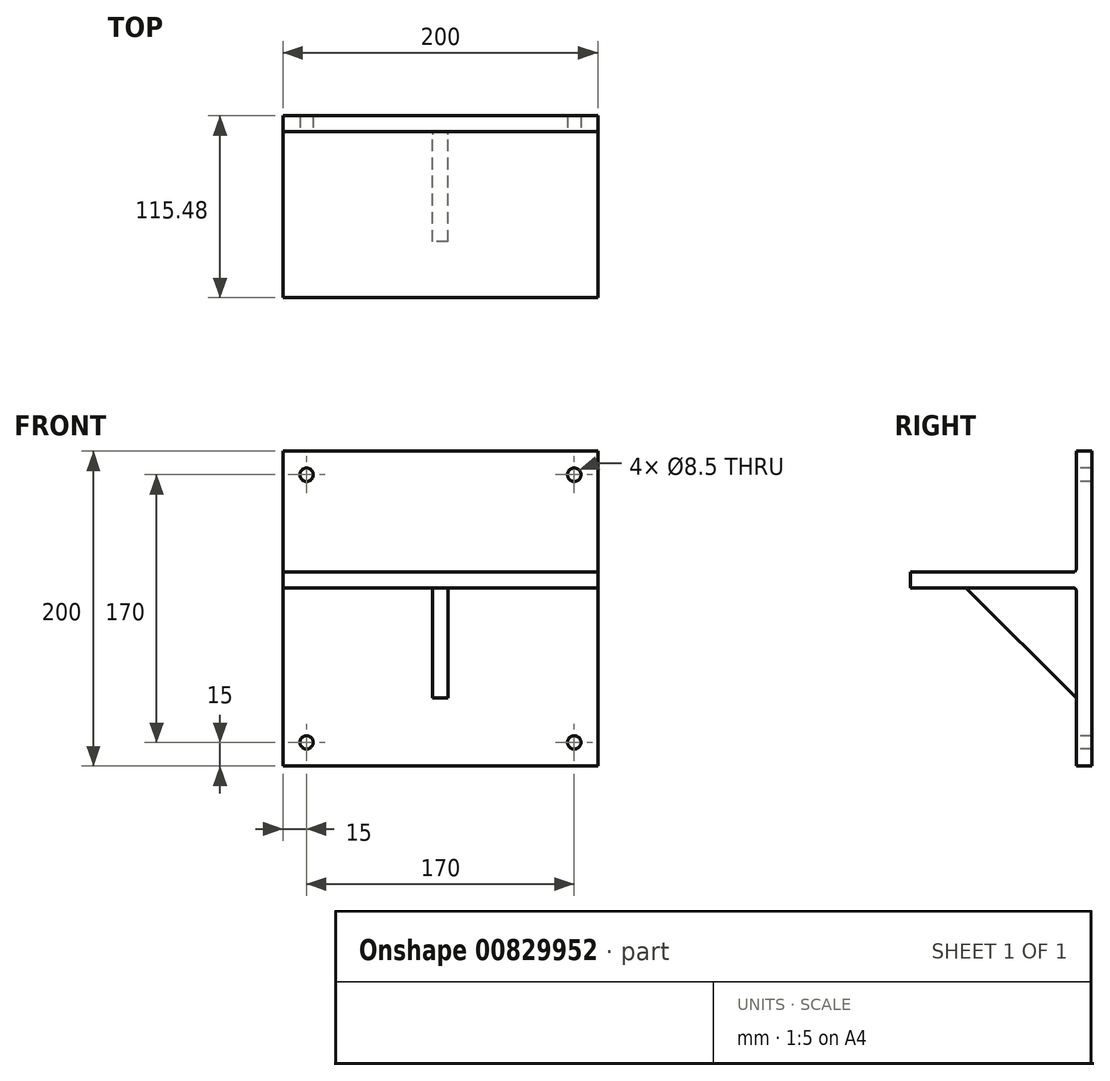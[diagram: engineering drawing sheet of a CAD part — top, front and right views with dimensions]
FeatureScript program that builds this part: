
annotation { "Feature Type Name" : "Feature", "Feature Type Description" : "" }
export const myFeature = defineFeature(function(context is Context, id is Id, definition is map)
    precondition{}
    {
        {
            var Q0;
            Q0=qCreatedBy(makeId("Right.planeOp"),FACE);
            var sketch = newSketch(context, id + "F0", { "sketchPlane" : qUnion([Q0])});
            skLineSegment(sketch, "E0", {"start": v(5, 81.8) * mm, "end": v(5, -118.2) * mm});
            skLineSegment(sketch, "E1", {"start": v(5, -118.2) * mm, "end": v(-5, -118.2) * mm});
            skLineSegment(sketch, "E2", {"start": v(5, 81.8) * mm, "end": v(-5, 81.8) * mm});
            skLineSegment(sketch, "E3", {"start": v(-5, 81.8) * mm, "end": v(-5, 5) * mm});
            skLineSegment(sketch, "E4", {"start": v(-5, -118.2) * mm, "end": v(-5, -5) * mm});
            skLineSegment(sketch, "E5", {"start": v(-5, -5) * mm, "end": v(-110.48, -5) * mm});
            skLineSegment(sketch, "E6", {"start": v(-110.48, -5) * mm, "end": v(-110.48, 5) * mm});
            skLineSegment(sketch, "E7", {"start": v(-110.48, 5) * mm, "end": v(-5, 5) * mm});
            skPoint(sketch, "E8.start.orphan", {"position": v(-5, -61.6) * mm});
            skSolve(sketch);
        }
        {
            var Q0;
            Q0 = qSketchRegion(id + "F0", true);
            extrude(context, id + "F1", {"entities" : qUnion([Q0]), "endBound" : BoundingType.SYMMETRIC, "depth" : 200 * mm, "offsetDistance" : 25.4 * mm});
        }
        {
            var Q0;
            Q0=makeQuery(id+"F1.opExtrude","SWEPT_FACE",FACE,{"disambiguationData":[OSD([sQuery(id+"F0.wireOp",EDGE,"E4")])]});
            var sketch = newSketch(context, id + "F2", { "sketchPlane" : qUnion([Q0])});
            skLineSegment(sketch, "E9", {"start": v(-5, -5) * mm, "end": v(-5, -75) * mm});
            skLineSegment(sketch, "E10", {"start": v(-5, -75) * mm, "end": v(5, -75) * mm});
            skLineSegment(sketch, "E11", {"start": v(5, -75) * mm, "end": v(5, -5) * mm});
            skLineSegment(sketch, "E12", {"start": v(5, -5) * mm, "end": v(-5, -5) * mm});
            skPoint(sketch, "E13.center.orphan", {"position": v(-85, -103.2) * mm});
            skPoint(sketch, "E14.center.orphan", {"position": v(92.52, -103.2) * mm});
            skSolve(sketch);
        }
        {
            var Q0;
            Q0=makeQuery(id+"F2.imprint","IMPRINT",FACE,{"disambiguationData":[TD([[makeQuery(id+"F2.imprint","IMPRINT",EDGE,{"derivedFrom":sQuery(id+"F2.wireOp",EDGE,"E9")}),1.0]])]});
            extrude(context, id + "F3", {"entities" : qUnion([Q0]), "operationType" : NewBodyOperationType.ADD, "depth" : 70 * mm, "offsetDistance" : 25.4 * mm});
        }
        {
            var Q0;
            Q0=makeQuery(id+"F3.opExtrude","SWEPT_FACE",FACE,{"disambiguationData":[OSD([sQuery(id+"F2.wireOp",EDGE,"E9")])]});
            var sketch = newSketch(context, id + "F4", { "sketchPlane" : qUnion([Q0])});
            skLineSegment(sketch, "E15", {"start": v(75, -5) * mm, "end": v(5, -75) * mm});
            skSolve(sketch);
        }
        {
            var Q0;
            Q0=makeQuery(id+"F4.imprint","IMPRINT",FACE,{"disambiguationData":[TD([[makeQuery(id+"F4.imprint","IMPRINT",EDGE,{"derivedFrom":sQuery(id+"F4.wireOp",EDGE,"E15")}),1.0]])]});
            extrude(context, id + "F5", {"entities" : qUnion([Q0]), "operationType" : NewBodyOperationType.REMOVE, "oppositeDirection" : true, "depth" : 10 * mm, "offsetDistance" : 25.4 * mm});
        }
        {
            var Q0;
            Q0=makeQuery(id+"F1.opExtrude","SWEPT_FACE",FACE,{"disambiguationData":[OSD([sQuery(id+"F0.wireOp",EDGE,"E4")])]});
            var sketch = newSketch(context, id + "F6", { "sketchPlane" : qUnion([Q0])});
            skCircle(sketch, "E16", {"center": v(-85, -103.2) * mm, "radius": 4.25 * mm});
            skCircle(sketch, "E17", {"center": v(85, -103.2) * mm, "radius": 4.25 * mm});
            skSolve(sketch);
        }
        {
            var Q0;
            Q0=makeQuery(id+"F6.imprint","IMPRINT",FACE,{"disambiguationData":[TD([[makeQuery(id+"F6.imprint","IMPRINT",EDGE,{"derivedFrom":sQuery(id+"F6.wireOp",EDGE,"E17")}),1.0]])]});
            var Q1;
            Q1=makeQuery(id+"F6.imprint","IMPRINT",FACE,{"disambiguationData":[TD([[makeQuery(id+"F6.imprint","IMPRINT",EDGE,{"derivedFrom":sQuery(id+"F6.wireOp",EDGE,"E16")}),1.0]])]});
            extrude(context, id + "F7", {"entities" : qUnion([Q0, Q1]), "operationType" : NewBodyOperationType.REMOVE, "oppositeDirection" : true, "depth" : 10 * mm, "offsetDistance" : 25.4 * mm});
        }
        {
            var Q0;
            Q0=makeQuery(id+"F1.opExtrude","SWEPT_FACE",FACE,{"disambiguationData":[OSD([sQuery(id+"F0.wireOp",EDGE,"E3")])]});
            var sketch = newSketch(context, id + "F8", { "sketchPlane" : qUnion([Q0])});
            skCircle(sketch, "E18", {"center": v(-85, 66.8) * mm, "radius": 4.25 * mm});
            skCircle(sketch, "E19", {"center": v(85, 66.8) * mm, "radius": 4.25 * mm});
            skSolve(sketch);
        }
        {
            var Q0;
            Q0=makeQuery(id+"F8.imprint","IMPRINT",FACE,{"disambiguationData":[TD([[makeQuery(id+"F8.imprint","IMPRINT",EDGE,{"derivedFrom":sQuery(id+"F8.wireOp",EDGE,"E18")}),1.0]])]});
            var Q1;
            Q1=makeQuery(id+"F8.imprint","IMPRINT",FACE,{"disambiguationData":[TD([[makeQuery(id+"F8.imprint","IMPRINT",EDGE,{"derivedFrom":sQuery(id+"F8.wireOp",EDGE,"E19")}),1.0]])]});
            extrude(context, id + "F9", {"entities" : qUnion([Q0, Q1]), "operationType" : NewBodyOperationType.REMOVE, "oppositeDirection" : true, "depth" : 10 * mm, "offsetDistance" : 25.4 * mm});
        }
        {
            var Q0;
            {var subQ0=sQuery(id+"F0.wireOp",EDGE,"E5");var subQ1=sQuery(id+"F0.wireOp",EDGE,"E4");Q0=makeQuery(id+"F3.boolean.opBoolean","SPLIT",EDGE,{"disambiguationData":[TD([makeQuery(id+"F3.opExtrude","SWEPT_FACE",FACE,{"disambiguationData":[OSD([sQuery(id+"F2.wireOp",EDGE,"E9")])]})])],"derivedFrom":makeQuery(id+"F1.opExtrude","SWEPT_EDGE",EDGE,{"disambiguationData":[OSD([subQ1,subQ0])]})});}
            var Q1;
            {var subQ0=sQuery(id+"F0.wireOp",EDGE,"E5");var subQ1=sQuery(id+"F0.wireOp",EDGE,"E4");Q1=makeQuery(id+"F3.boolean.opBoolean","SPLIT",EDGE,{"disambiguationData":[TD([makeQuery(id+"F3.opExtrude","SWEPT_FACE",FACE,{"disambiguationData":[OSD([sQuery(id+"F2.wireOp",EDGE,"E11")])]})])],"derivedFrom":makeQuery(id+"F1.opExtrude","SWEPT_EDGE",EDGE,{"disambiguationData":[OSD([subQ1,subQ0])]})});}
            var Q2;
            Q2=makeQuery(id+"F3.opExtrude","SWEPT_EDGE",EDGE,{"disambiguationData":[OSD([sQuery(id+"F0.wireOp",EDGE,"E4"),sQuery(id+"F0.wireOp",EDGE,"E5"),sQuery(id+"F2.wireOp",EDGE,"E9"),sQuery(id+"F2.wireOp",EDGE,"E12")])]});
            var Q3;
            Q3=makeQuery(id+"F3.opExtrude","CAP_EDGE",EDGE,{"disambiguationData":[OSD([sQuery(id+"F2.wireOp",EDGE,"E9")])],"isStart":true});
            var Q4;
            Q4=makeQuery(id+"F3.opExtrude","CAP_EDGE",EDGE,{"disambiguationData":[OSD([sQuery(id+"F2.wireOp",EDGE,"E11")])],"isStart":true});
            var Q5;
            Q5=makeQuery(id+"F3.opExtrude","SWEPT_EDGE",EDGE,{"disambiguationData":[OSD([sQuery(id+"F0.wireOp",EDGE,"E4"),sQuery(id+"F0.wireOp",EDGE,"E5"),sQuery(id+"F2.wireOp",EDGE,"E11"),sQuery(id+"F2.wireOp",EDGE,"E12")])]});
            var Q6;
            Q6=makeQuery(id+"F1.opExtrude","SWEPT_EDGE",EDGE,{"disambiguationData":[OSD([sQuery(id+"F0.wireOp",EDGE,"E3"),sQuery(id+"F0.wireOp",EDGE,"E7")])]});
            fillet(context, id + "F10", {"entities" : qUnion([Q0, Q1, Q2, Q3, Q4, Q5, Q6]), "radius" : 2 * mm, "tangentPropagation" : true, "allowEdgeOverflow" : false});
        }
    });
